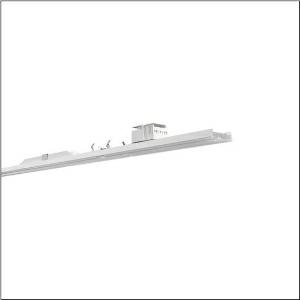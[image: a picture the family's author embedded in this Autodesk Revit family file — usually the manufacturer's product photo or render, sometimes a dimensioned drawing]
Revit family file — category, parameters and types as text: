
# Revit family: licross_r__21_recessed_mo_52tl18dnd75f_1d51
name_source: partatom
category: Lighting Fixtures
units: mm (PartAtom-declared; Revit-internal decimal feet)

## family parameters
Cut with Voids When Loaded = No
Host = Face
Light Source = No
Part Type = Normal
Room Calculation Point = No
Round Connector Dimension = Use Diameter
Shared = No

## types (1)
- --- (1 x LED, 7730 lm, 59.8 W, 4000K)
    Apparent Load = 60 VA
    CIE Flux Codes = 79 95 99 100 100
    Color Rendering = 90
    Color Temperature = 4000K
    Default Elevation = 1800 mm
    Description = Licross® 21 Recessed MO, luminaire insert, of sheet steel, galvanised, coil coated, white, length: 1.500mm, width: 66mm, height: 67mm, LED rated luminous flux: 7.730lm, light colour: 940, control gear: DALI 2, control gear: ECG DALI, with plug, 5-pole, with phase selection, mains connection: 220..240V, AC, 50/60Hz, halogen-free wiring, primary optical cover: cover, of PMMA, light emission: direct distribution, protection rating (complete): IP40, insulation class (complete): insulation class I (protective earthing), certification: CE, ENEC, VDE, UKCA, protection symbol: D if used in an environment without relevant dust loads with corresponding accessories, permissible ambient temperature for indoor applications: -25..+35°C, corresponds to IFS (International Featured Standards) requirements for safety and quality in the food industry, reducing of maximum allowable ambient temperature of 5°C with ceiling mounting, packaging unit: 1 piece
    Height = 58 mm
    Lamp = 1 x LED
    Lamp Light Flux = 7730 lm
    Lamp Power = 59.8 W
    Lamp count = 1
    Length = 1500 mm
    Luminous efficacy = 129 lm/W
    Manufacturer = Siteco
    ModVariant = No
    Model = 52TL18DND75F
    Mounting Place = Ceiling
    Mounting Type = Pendant
    Number of Poles = 1
    OnlyDefault = Yes
    Power Factor = 1
    Product Name = Licross® 21 Recessed MO
    Product group = luminaire insert
    ProductGroupID = 902
    Protection Class = Protection class I
    Protection Degree = IP 40
    RLX_Detail_Level = 1
    RlxData = <blob elided: 22469 chars, md5=bc786587>
    Socket = socket
    Standby Power = 0 W
    System Light Flux = 7730 lm
    System Power = 60 W
    Type Comments = factory setting: luminous flux: 100 % | dim-lin: 254 | 405 mA
    Type Image = l_1266722.jpg
    URL = http://relux.com
    VarID = @adj_099807
    Voltage = 0 V
    Weight = 0.00 kg
    Width = 66 mm

## geometry (parser evidence)
native form markers: Blend x4, Sweep x10
no freeform markers — native parametric forms only
